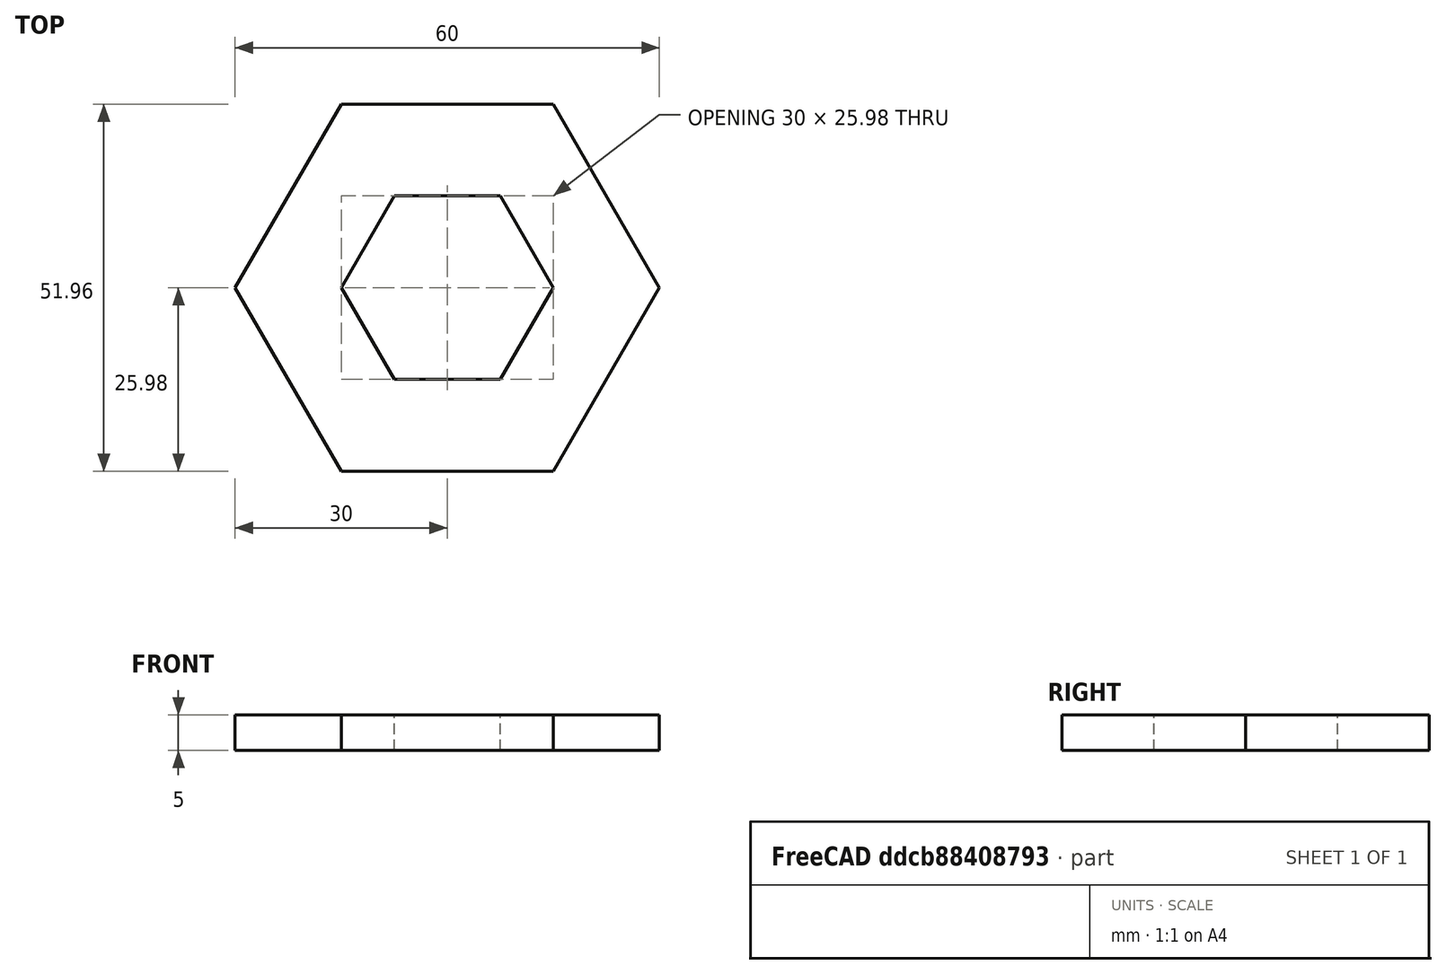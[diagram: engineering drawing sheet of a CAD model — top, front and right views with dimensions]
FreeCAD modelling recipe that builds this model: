
FCSTD DOCUMENT  (FreeCAD 0.19R)
Label: random-tiles
License: All rights reserved
LicenseURL: http://en.wikipedia.org/wiki/All_rights_reserved
objects: Sketcher::SketchObject×1, Part::Extrusion×1
note: 2 computed .brp shape members not serialized (recipe doc carries the construction recipe); baked Part::Feature solids carry a one-line shape summary decoded from their .brp

FEATURE [Sketcher::SketchObject] Sketch
  FullyConstrained = true
  sketch-geometry (14):
    g0: LineSegment StartX=15 StartY=0 StartZ=0 EndX=7.5 EndY=12.9904 EndZ=0
    g1: LineSegment StartX=7.5 StartY=12.9904 StartZ=0 EndX=-7.5 EndY=12.9904 EndZ=0
    g2: LineSegment StartX=-7.5 StartY=12.9904 StartZ=0 EndX=-15 EndY=4.1194e-12 EndZ=0
    g3: LineSegment StartX=-15 StartY=4.1194e-12 StartZ=0 EndX=-7.5 EndY=-12.9904 EndZ=0
    g4: LineSegment StartX=-7.5 StartY=-12.9904 StartZ=0 EndX=7.5 EndY=-12.9904 EndZ=0
    g5: LineSegment StartX=7.5 StartY=-12.9904 StartZ=0 EndX=15 EndY=0 EndZ=0
    g6: Circle CenterX=0 CenterY=0 CenterZ=0 NormalX=0 NormalY=0 NormalZ=1 AngleXU=0 Radius=15
    g7: LineSegment StartX=30 StartY=0 StartZ=0 EndX=15 EndY=25.9808 EndZ=0
    g8: LineSegment StartX=15 StartY=25.9808 StartZ=0 EndX=-15 EndY=25.9808 EndZ=0
    g9: LineSegment StartX=-15 StartY=25.9808 StartZ=0 EndX=-30 EndY=-8.58869e-11 EndZ=0
    g10: LineSegment StartX=-30 StartY=-8.58869e-11 StartZ=0 EndX=-15 EndY=-25.9808 EndZ=0
    g11: LineSegment StartX=-15 StartY=-25.9808 StartZ=0 EndX=15 EndY=-25.9808 EndZ=0
    g12: LineSegment StartX=15 StartY=-25.9808 StartZ=0 EndX=30 EndY=0 EndZ=0
    g13: Circle CenterX=-1e-16 CenterY=0 CenterZ=0 NormalX=0 NormalY=0 NormalZ=1 AngleXU=0 Radius=30
  constraints (32):
    c: Coincident(g0,g1)
    c: Coincident(g1,g2)
    c: Coincident(g2,g3)
    c: Coincident(g3,g4)
    c: Coincident(g4,g5)
    c: Coincident(g5,g0)
    c: Equal(g0, g1-g5) x5
    c: PointOnObject(g0,g6)
    c: PointOnObject(g1,g6)
    c: PointOnObject(g2,g6)
    c: PointOnObject(g3,g6)
    c: PointOnObject(g4,g6)
    c: PointOnObject(g5,g6)
    c: Coincident(g6,g-1)
    c: PointOnObject(g5,g-1)
    c: Coincident(g7,g8)
    c: Coincident(g8,g9)
    c: Coincident(g9,g10)
    c: Coincident(g10,g11)
    c: Coincident(g11,g12)
    c: Coincident(g12,g7)
    c: Equal(g7, g8-g12) x5
    c: PointOnObject(g7,g13)
    c: PointOnObject(g8,g13)
    c: PointOnObject(g9,g13)
    c: PointOnObject(g10,g13)
    c: PointOnObject(g11,g13)
    c: PointOnObject(g12,g13)
    c: Coincident(g13,g-1)
    c: PointOnObject(g12,g-1)
    c: Radius(g6) = 15  'R1'
    c: Radius(g13) = 30  'R2'
FEATURE [Part::Extrusion] Extrude  label="Tile"
  Base = -> Sketch
  Dir = (0,0,1)
  DirMode = 2
  FaceMakerClass = Part::FaceMakerBullseye
  LengthFwd = 5
  LengthRev = 0
  Solid = true
  Symmetric = false
